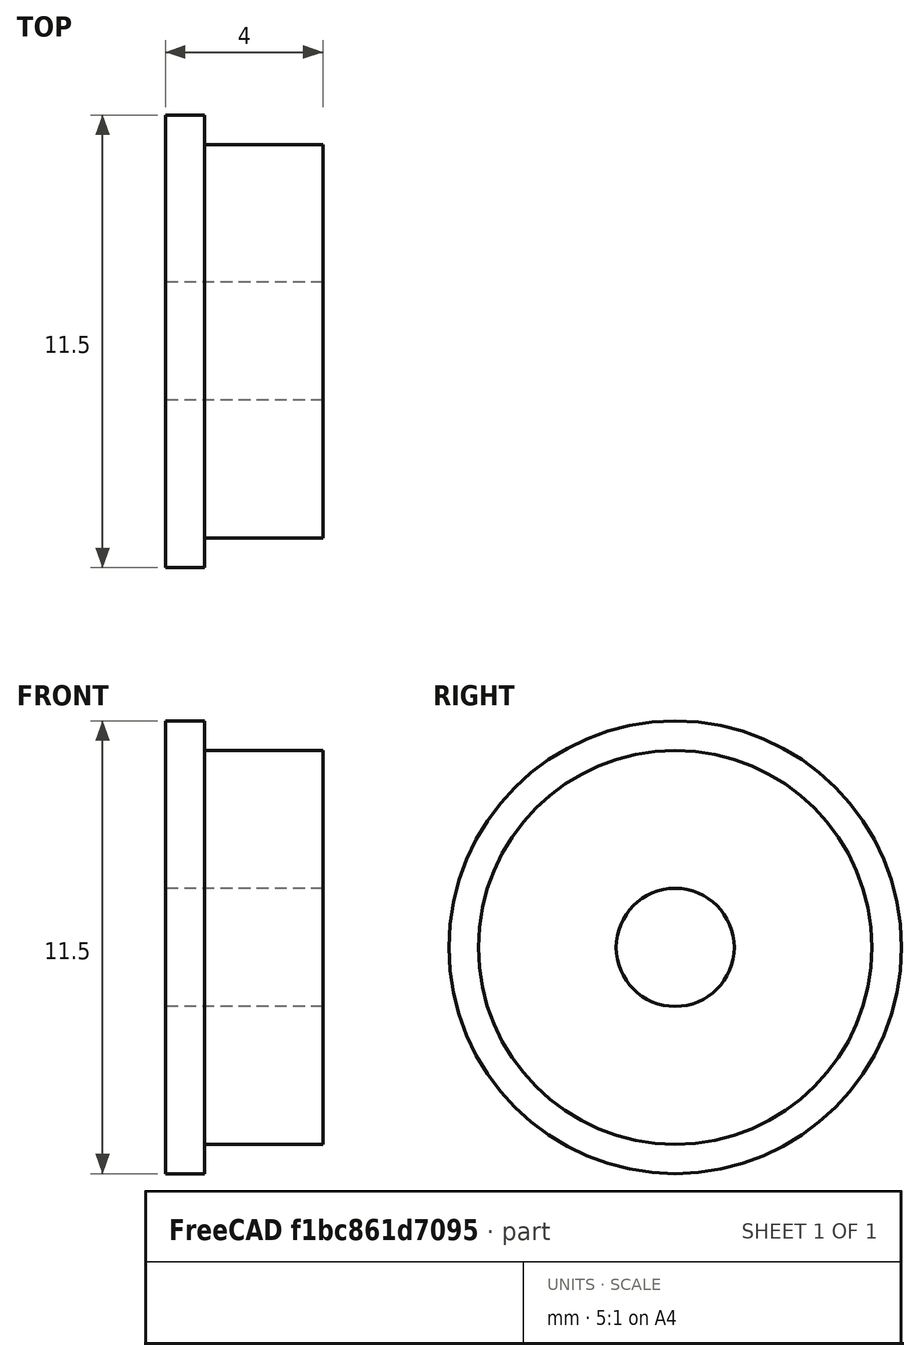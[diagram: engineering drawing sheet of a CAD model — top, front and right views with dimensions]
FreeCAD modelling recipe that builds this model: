
FCSTD DOCUMENT  (FreeCAD 0.18R16131 (Git))
Label: F623ZZ Ball Bearing
License: All rights reserved
LicenseURL: http://en.wikipedia.org/wiki/All_rights_reserved
objects: Sketcher::SketchObject×1, PartDesign::Revolution×1, PartDesign::Body×1
note: 4 computed .brp shape members not serialized (recipe doc carries the construction recipe); baked Part::Feature solids carry a one-line shape summary decoded from their .brp

FEATURE [Sketcher::SketchObject] Sketch
  MapMode = 5
  Support = -> [XY_Plane]
  sketch-geometry (7):
    g0: LineSegment StartX=0 StartY=1.5 StartZ=0 EndX=0 EndY=5.75 EndZ=0
    g1: LineSegment StartX=0 StartY=5.75 StartZ=0 EndX=1 EndY=5.75 EndZ=0
    g2: LineSegment StartX=1 StartY=5.75 StartZ=0 EndX=1 EndY=5 EndZ=0
    g3: LineSegment StartX=1 StartY=5 StartZ=0 EndX=4 EndY=5 EndZ=0
    g4: LineSegment StartX=4 StartY=5 StartZ=0 EndX=4 EndY=1.5 EndZ=0
    g5: LineSegment StartX=4 StartY=1.5 StartZ=0 EndX=0 EndY=1.5 EndZ=0
    g6: LineSegment [constr] StartX=0 StartY=0 StartZ=0 EndX=8.0448 EndY=0 EndZ=0
  constraints (20):
    c: PointOnObject(g0,g-2)
    c: Coincident(g0,g1)
    c: Horizontal(g1)
    c: Coincident(g1,g2)
    c: Vertical(g2)
    c: Coincident(g2,g3)
    c: Horizontal(g3)
    c: Coincident(g3,g4)
    c: Vertical(g4)
    c: Coincident(g4,g5)
    c: Horizontal(g5)
    c: Coincident(g0,g5)
    c: DistanceY(g-1,g0) = 5.75
    c: DistanceY(g-1,g3) = 5
    c: DistanceX(g5,g5) = 4
    c: Vertical(g0)
    c: DistanceY(g-1,g0) = 1.5
    c: DistanceX(g1,g1) = 1
    c: Coincident(g6,g-1)
    c: PointOnObject(g6,g-1)
FEATURE [PartDesign::Revolution] Revolution
  Angle = 360
  Axis = (1,0,0)
  Base = (0,0,0)
  Profile = -> Sketch
  ReferenceAxis = -> X_Axis
  Reversed = true
FEATURE [PartDesign::Body] Body
  Group = -> [Sketch,Revolution]
  Origin = -> Origin
  Tip = -> Revolution
